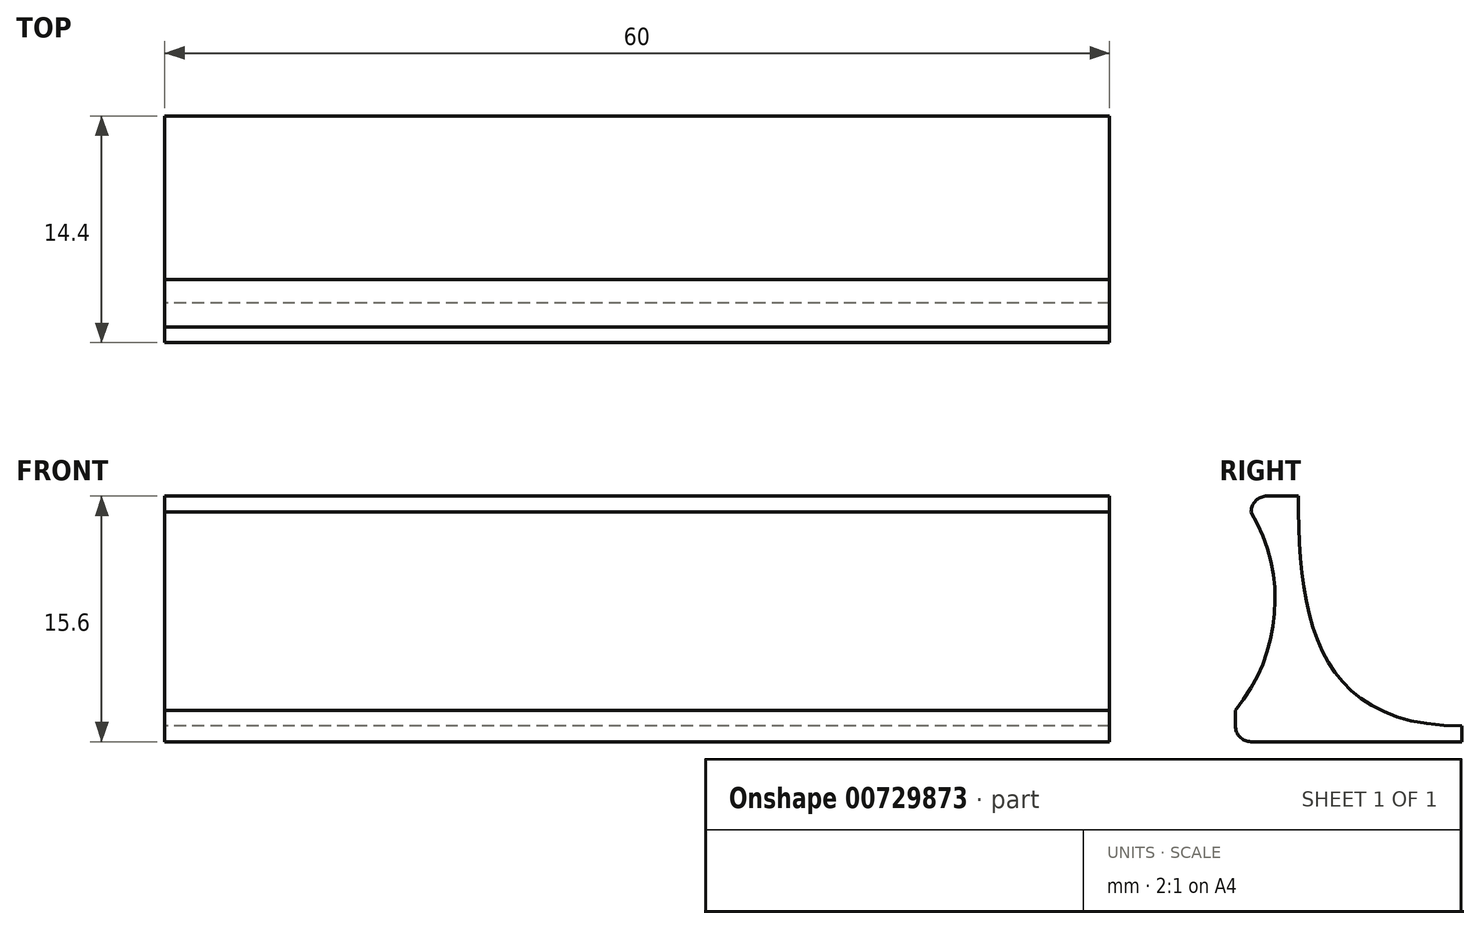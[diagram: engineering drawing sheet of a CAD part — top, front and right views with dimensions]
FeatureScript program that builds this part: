
annotation { "Feature Type Name" : "Feature", "Feature Type Description" : "" }
export const myFeature = defineFeature(function(context is Context, id is Id, definition is map)
    precondition{}
    {
        {
            var Q0;
            Q0=qCreatedBy(makeId("Right.planeOp"),FACE);
            var sketch = newSketch(context, id + "F0", { "sketchPlane" : qUnion([Q0])});
            skLineSegment(sketch, "E0.bottom", {"start": v(-3.5, 6.59) * mm, "end": v(-5.5, 6.59) * mm});
            skLineSegment(sketch, "E0.top", {"start": v(6.9, -9.01) * mm, "end": v(-6.5, -9.01) * mm});
            skLineSegment(sketch, "E0.left", {"start": v(6.9, -8.01) * mm, "end": v(6.9, -9.01) * mm});
            skPoint(sketch, "E0.middle", {"position": v(0, 0) * mm});
            skLineSegment(sketch, "E1", {"start": v(-3.5, 6.59) * mm, "end": v(-3.5, -8.01) * mm});
            skLineSegment(sketch, "E2", {"start": v(-3.5, -8.01) * mm, "end": v(6.9, -8.01) * mm, "construction": true});
            skArc(sketch, "E3", {"start": v(-7.5, -7.01) * mm, "mid": v(-5.01, -0.87) * mm, "end": v(-6.5, 5.59) * mm});
            skLineSegment(sketch, "E4", {"start": v(-6.5, 5.59) * mm, "end": v(-6.5, 5.59) * mm});
            skLineSegment(sketch, "E5", {"start": v(-7.5, -7.01) * mm, "end": v(-7.5, -8.01) * mm});
            skPoint(sketch, "E6.visualSharp", {"position": v(-6.5, 6.59) * mm});
            skArc(sketch, "E6.filletArc", {"start": v(-5.5, 6.59) * mm, "mid": v(-6.21, 6.3) * mm, "end": v(-6.5, 5.59) * mm});
            skPoint(sketch, "E7.visualSharp", {"position": v(-7.5, -9.01) * mm});
            skArc(sketch, "E7.filletArc", {"start": v(-7.5, -8.01) * mm, "mid": v(-7.21, -8.72) * mm, "end": v(-6.5, -9.01) * mm});
            skFitSpline(sketch, "E8", {"points": [v(-3.5, 6.59) * mm, v(6.9, -8.01) * mm], "startDerivative": vector(0, -23.27) * mm, "endDerivative": vector(27.93, 0) * mm});
            skLineSegment(sketch, "E9", {"start": v(-3.5, -8.01) * mm, "end": v(-3.5, -9.01) * mm});
            skSolve(sketch);
        }
        {
            var Q0;
            Q0 = qSketchRegion(id + "F0", true);
            extrude(context, id + "F1", {"entities" : qUnion([Q0]), "depth" : 60 * mm, "offsetDistance" : 25 * mm});
        }
    });
